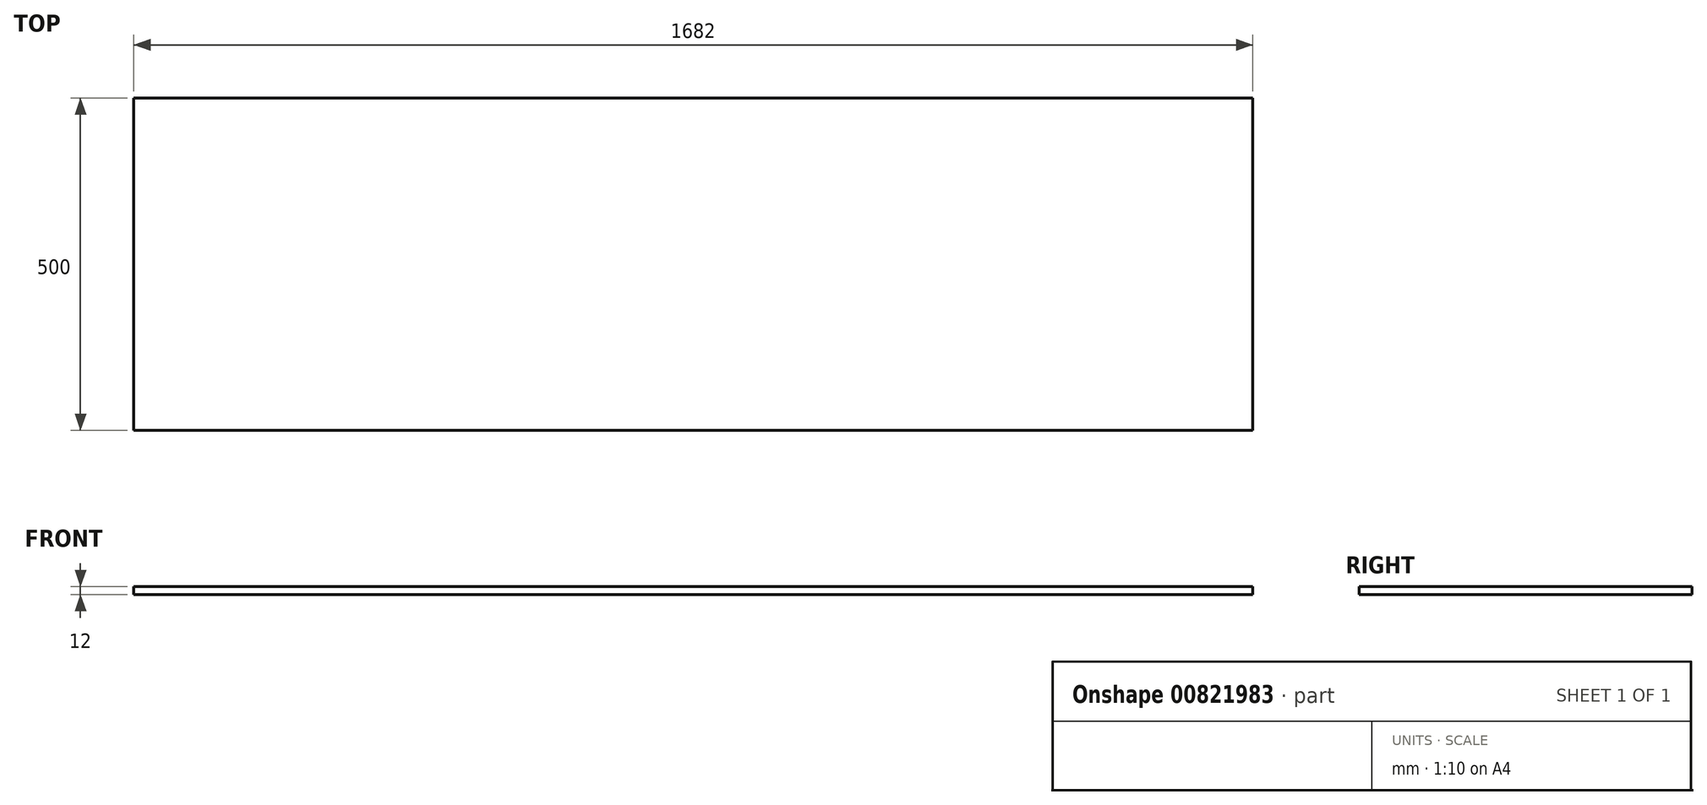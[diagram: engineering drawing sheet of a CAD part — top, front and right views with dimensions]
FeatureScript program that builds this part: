
annotation { "Feature Type Name" : "Feature", "Feature Type Description" : "" }
export const myFeature = defineFeature(function(context is Context, id is Id, definition is map)
    precondition{}
    {
        {
            var Q0;
            Q0=qCreatedBy(makeId("Top.planeOp"),FACE);
            var sketch = newSketch(context, id + "F0", { "sketchPlane" : qUnion([Q0])});
            skLineSegment(sketch, "E0.bottom", {"start": v(-1575.03, 457.65) * mm, "end": v(106.97, 457.65) * mm});
            skLineSegment(sketch, "E0.top", {"start": v(-1575.03, -42.35) * mm, "end": v(106.97, -42.35) * mm});
            skLineSegment(sketch, "E0.left", {"start": v(-1575.03, 457.65) * mm, "end": v(-1575.03, -42.35) * mm});
            skLineSegment(sketch, "E0.right", {"start": v(106.97, 457.65) * mm, "end": v(106.97, -42.35) * mm});
            skSolve(sketch);
        }
        {
            var Q0;
            Q0=makeQuery(id+"F0.imprint","IMPRINT",FACE,{"disambiguationData":[TD([[makeQuery(id+"F0.imprint","IMPRINT",EDGE,{"derivedFrom":sQuery(id+"F0.wireOp",EDGE,"E0.bottom")}),-1.0]])]});
            extrude(context, id + "F1", {"entities" : qUnion([Q0]), "depth" : 12 * mm, "offsetDistance" : 25 * mm});
        }
    });
